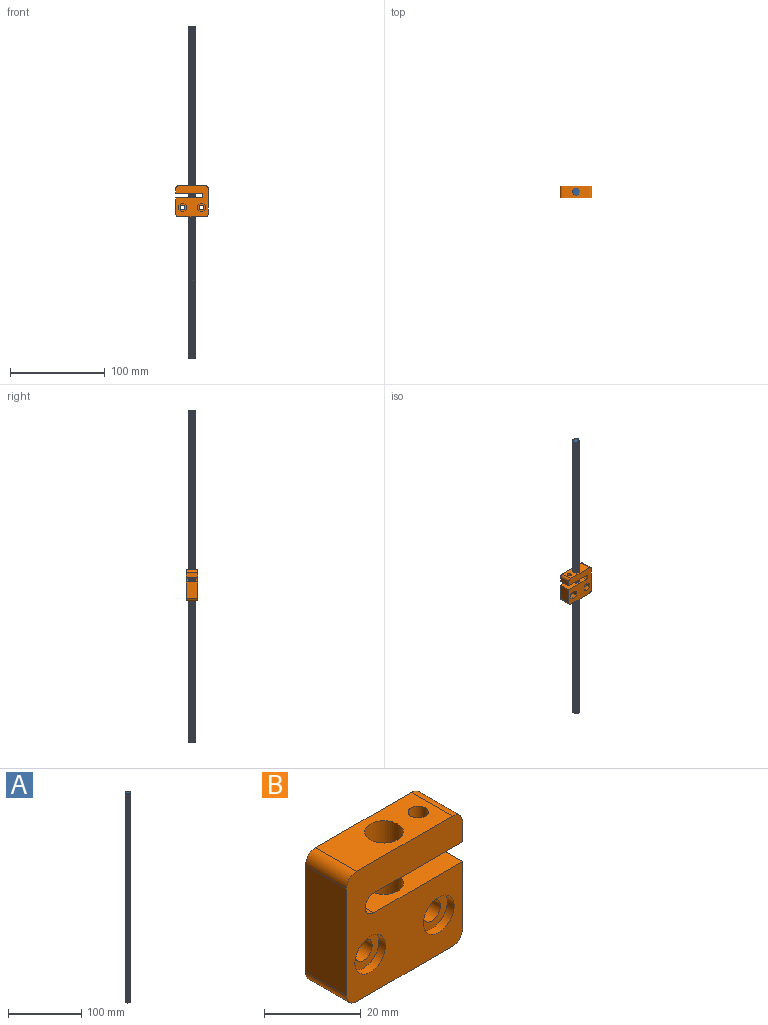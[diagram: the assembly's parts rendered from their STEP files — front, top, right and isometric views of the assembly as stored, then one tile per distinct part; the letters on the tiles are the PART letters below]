
ASSEMBLY  parts=2 mates=1
PART A: 27 faces, bbox 8x8x351 mm
  f0: cylinder r=4mm len=349mm, axis (0,0,-1), area 1253.1mm2, adj f3,f6,f12,f14,f21
  f1: cylinder r=4mm len=349mm, axis (0,0,-1), area 1253.1mm2, adj f5,f6,f16,f18,f25
  f2: plane 7x7mm, normal (0,0,-1), area 33.4mm2, adj f3,f4,f5,f9,f11,f12,f13,f15
  f3: cone r=4mm half-angle=45deg, axis (0,0,1), area 2.1mm2, adj f0,f2,f12,f21
  f4: cone r=4mm half-angle=45deg, axis (0,0,1), area 2.1mm2, adj f2,f8,f13,f24
  f5: cone r=4mm half-angle=45deg, axis (0,0,1), area 2.1mm2, adj f1,f2,f16,f25
  f6: cone r=3.5mm half-angle=45deg, axis (0,0,-1), area 14.6mm2, adj f0,f1,f7,f8,f10,f13,f14,f17
  f7: cylinder r=4mm len=349mm, axis (0,0,-1), area 1253.1mm2, adj f6,f9,f17,f20,f22
  f8: cylinder r=4mm len=349mm, axis (0,0,-1), area 1253.1mm2, adj f4,f6,f13,f24,f26
  f9: cone r=4mm half-angle=45deg, axis (0,0,1), area 2.1mm2, adj f2,f7,f17,f20
  f10: plane 7x7mm, normal (0,0,1), area 38.5mm2, adj f6
  f11: cylinder r=3mm len=349.99mm, axis (0,0,1), area 1978.7mm2, adj f2,f12,f13,f14
  f12: bspline ~350x8mm, area 1020.3mm2, adj f0,f2,f3,f11,f14
  f13: bspline ~351x8mm, area 1027.4mm2, adj f2,f4,f6,f8,f11,f14
  f14: plane 1x1mm, normal (0,-1,0), area 0.9mm2, adj f0,f6,f11,f12,f13
  f15: cylinder r=3mm len=349.99mm, axis (0,0,1), area 1978.7mm2, adj f2,f16,f17,f18
  f16: bspline ~349x8mm, area 1021.8mm2, adj f1,f2,f5,f15,f18
  f17: bspline ~351x8mm, area 1021.9mm2, adj f2,f6,f7,f9,f15,f18
  f18: plane 1x1mm, normal (0,1,0), area 0.9mm2, adj f1,f6,f15,f16,f17
  f19: cylinder r=3mm len=349.99mm, axis (0,0,1), area 1978.7mm2, adj f2,f20,f21,f22
  f20: bspline ~350x8mm, area 1020.3mm2, adj f2,f7,f9,f19,f22
  f21: bspline ~351x8mm, area 1027.4mm2, adj f0,f2,f3,f6,f19,f22
  f22: plane 1x1mm, normal (-1,0,0), area 0.9mm2, adj f6,f7,f19,f20,f21
  f23: cylinder r=3mm len=349.99mm, axis (0,0,1), area 1978.7mm2, adj f2,f24,f25,f26
  f24: bspline ~349x8mm, area 1021.8mm2, adj f2,f4,f8,f23,f26
  f25: bspline ~351x8mm, area 1021.9mm2, adj f1,f2,f5,f6,f23,f26
  f26: plane 1x1mm, normal (1,0,0), area 0.9mm2, adj f6,f8,f23,f24,f25
PART B: 37 faces, bbox 34x12x33 mm
  f0: cylinder r=2.1mm len=8mm, axis (0,0,1), area 105.6mm2, adj f13,f31
  f1: cylinder r=2.5mm len=12mm, axis (0,1,0), area 94.2mm2, adj f10,f12,f31,f32
  f2: cylinder r=4.5mm len=9mm, axis (0,-1,0), area 56.5mm2, adj f10,f30
  f3: cylinder r=4.5mm len=9mm, axis (0,-1,0), area 56.5mm2, adj f10,f29
  f4: cylinder r=4mm len=20mm, axis (0,0,1), area 502.7mm2, adj f14,f32
  f5: cylinder r=2.55mm len=5.1mm, axis (0,1,0), area 80.1mm2, adj f22,f29
  f6: cylinder r=2.55mm len=5.1mm, axis (0,1,0), area 80.1mm2, adj f15,f30
  f7: cylinder r=4mm len=8mm, axis (0,0,1), area 201.1mm2, adj f13,f31
  f8: plane 12x5mm, normal (1,0,0), area 60mm2, adj f10,f12,f31,f35
  f9: plane 27x12mm, normal (-1,0,0), area 324mm2, adj f10,f12,f33,f36
  f10: plane 34x33mm, normal (0,-1,0), area 847.2mm2, adj f1,f2,f3,f8,f9,f11,f13,f14
  f11: plane 17x12mm, normal (1,0,0), area 204mm2, adj f10,f12,f32,f34
  f12: plane 34x33mm, normal (0,1,0), area 863.6mm2, adj f1,f8,f9,f11,f13,f14,f16,f17
  f13: plane 28x12mm, normal (0,0,1), area 271.9mm2, adj f0,f7,f10,f12,f35,f36
  f14: plane 28x12mm, normal (0,0,-1), area 285.7mm2, adj f4,f10,f12,f33,f34
  f15: plane 9.24x8mm, normal (0,1,0), area 35mm2, adj f6,f16,f17,f18,f19,f20,f21
  f16: plane 5x4mm, normal (-0.5,0,0.87), area 23.1mm2, adj f12,f15,f17,f21
  f17: plane 5x4.62mm, normal (-1,0,0), area 23.1mm2, adj f12,f15,f16,f18
  f18: plane 5x4mm, normal (-0.5,0,-0.87), area 23.1mm2, adj f12,f15,f17,f19
  f19: plane 5x4mm, normal (0.5,0,-0.87), area 23.1mm2, adj f12,f15,f18,f20
  f20: plane 5x4.62mm, normal (1,0,0), area 23.1mm2, adj f12,f15,f19,f21
  f21: plane 5x4mm, normal (0.5,0,0.87), area 23.1mm2, adj f12,f15,f16,f20
  f22: plane 9.24x8mm, normal (0,1,0), area 35mm2, adj f5,f23,f24,f25,f26,f27,f28
  f23: plane 5x4.62mm, normal (1,0,0), area 23.1mm2, adj f12,f22,f24,f28
  f24: plane 5x4mm, normal (0.5,0,0.87), area 23.1mm2, adj f12,f22,f23,f25
  f25: plane 5x4mm, normal (-0.5,0,0.87), area 23.1mm2, adj f12,f22,f24,f26
  f26: plane 5x4.62mm, normal (-1,0,0), area 23.1mm2, adj f12,f22,f25,f27
  f27: plane 5x4mm, normal (-0.5,0,-0.87), area 23.1mm2, adj f12,f22,f26,f28
  f28: plane 5x4mm, normal (0.5,0,-0.87), area 23.1mm2, adj f12,f22,f23,f27
  f29: plane 9x9mm, normal (0,-1,0), area 43.2mm2, adj f3,f5
  f30: plane 9x9mm, normal (0,-1,0), area 43.2mm2, adj f2,f6
  f31: plane 26x12mm, normal (0,0,-1), area 247.9mm2, adj f0,f1,f7,f8,f10,f12
  f32: plane 26x12mm, normal (0,0,1), area 261.7mm2, adj f1,f4,f10,f11,f12
  f33: cylinder r=3mm len=12mm, axis (0,-1,0), area 56.5mm2, adj f9,f10,f12,f14
  f34: cylinder r=3mm len=12mm, axis (0,1,0), area 56.5mm2, adj f10,f11,f12,f14
  f35: cylinder r=3mm len=12mm, axis (0,-1,0), area 56.5mm2, adj f8,f10,f12,f13
  f36: cylinder r=3mm len=12mm, axis (0,1,0), area 56.5mm2, adj f9,f10,f12,f13
PLACE A rot(axis=(-0.97,-0.25,0),180deg) t=(-202.68,114.21,252.84)mm
PLACE B rot(axis=(0,0,-1),179.7deg) t=(-202.68,114.21,51.52)mm
MATE cylindrical B.f4 <-> A.f0  axis (0,0,1) through (-202.68,114.21,84.52)mm
